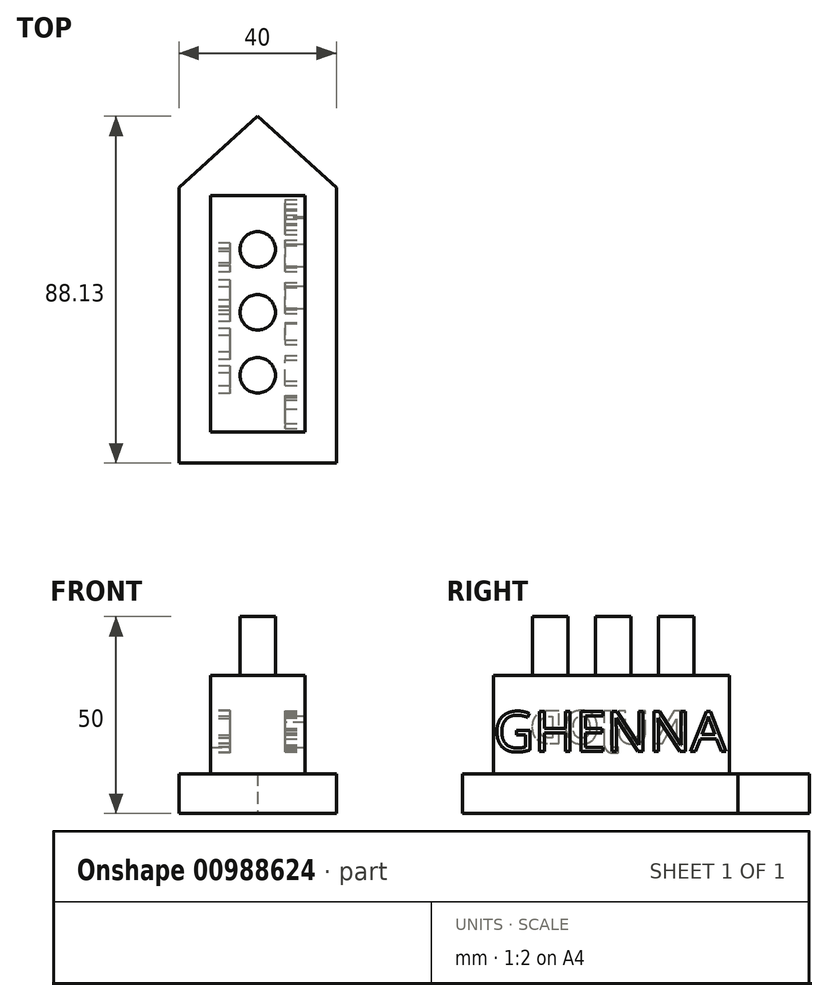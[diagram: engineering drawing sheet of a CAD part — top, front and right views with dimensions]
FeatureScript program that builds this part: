
annotation { "Feature Type Name" : "Feature", "Feature Type Description" : "" }
export const myFeature = defineFeature(function(context is Context, id is Id, definition is map)
    precondition{}
    {
        {
            var Q0;
            Q0=qCreatedBy(makeId("Top.planeOp"),FACE);
            var sketch = newSketch(context, id + "F0", { "sketchPlane" : qUnion([Q0])});
            skLineSegment(sketch, "E0", {"start": v(-20, 21.16) * mm, "end": v(-20, -48.84) * mm});
            skLineSegment(sketch, "E1", {"start": v(-20, -48.84) * mm, "end": v(20, -48.84) * mm});
            skLineSegment(sketch, "E2", {"start": v(20, -48.84) * mm, "end": v(20, 21.16) * mm});
            skLineSegment(sketch, "E3", {"start": v(-20, 21.16) * mm, "end": v(0, 39.3) * mm});
            skLineSegment(sketch, "E4", {"start": v(0, 39.3) * mm, "end": v(20, 21.16) * mm});
            skSolve(sketch);
        }
        {
            var Q0;
            Q0 = qSketchRegion(id + "F0", true);
            extrude(context, id + "F1", {"entities" : qUnion([Q0]), "depth" : 10 * mm, "offsetDistance" : 25 * mm});
        }
        {
            var Q0;
            Q0=makeQuery(id+"F1.opExtrude","CAP_FACE",FACE,{"disambiguationData":[OSD([sQuery(id+"F0.wireOp",EDGE,"E0"),sQuery(id+"F0.wireOp",EDGE,"E1"),sQuery(id+"F0.wireOp",EDGE,"E2"),sQuery(id+"F0.wireOp",EDGE,"E3"),sQuery(id+"F0.wireOp",EDGE,"E4")])],"isStart":false});
            var sketch = newSketch(context, id + "F2", { "sketchPlane" : qUnion([Q0])});
            skLineSegment(sketch, "E5", {"start": v(-12, 19.07) * mm, "end": v(-12, -40.93) * mm});
            skLineSegment(sketch, "E6", {"start": v(-12, -40.93) * mm, "end": v(12, -40.93) * mm});
            skLineSegment(sketch, "E7", {"start": v(12, -40.93) * mm, "end": v(12, 19.07) * mm});
            skLineSegment(sketch, "E8", {"start": v(12, 19.07) * mm, "end": v(-12, 19.07) * mm});
            skSolve(sketch);
        }
        {
            var Q0;
            Q0 = qSketchRegion(id + "F2", true);
            extrude(context, id + "F3", {"entities" : qUnion([Q0]), "operationType" : NewBodyOperationType.ADD, "depth" : 25 * mm, "offsetDistance" : 25 * mm});
        }
        {
            var Q0;
            Q0=makeQuery(id+"F3.opExtrude","CAP_FACE",FACE,{"disambiguationData":[OSD([sQuery(id+"F2.wireOp",EDGE,"E5"),sQuery(id+"F2.wireOp",EDGE,"E6"),sQuery(id+"F2.wireOp",EDGE,"E7"),sQuery(id+"F2.wireOp",EDGE,"E8")])],"isStart":false});
            var sketch = newSketch(context, id + "F4", { "sketchPlane" : qUnion([Q0])});
            skCircle(sketch, "E9", {"center": v(0, 5.44) * mm, "radius": 4.5 * mm});
            skCircle(sketch, "E10", {"center": v(0, -10.56) * mm, "radius": 4.5 * mm});
            skCircle(sketch, "E11", {"center": v(0, -26.56) * mm, "radius": 4.5 * mm});
            skSolve(sketch);
        }
        {
            var Q0;
            Q0 = qSketchRegion(id + "F4", true);
            extrude(context, id + "F5", {"entities" : qUnion([Q0]), "depth" : 15 * mm, "offsetDistance" : 25 * mm});
        }
        {
            var Q0;
            Q0=makeQuery(id+"F3.opExtrude","SWEPT_FACE",FACE,{"disambiguationData":[OSD([sQuery(id+"F2.wireOp",EDGE,"E5")])]});
            var sketch = newSketch(context, id + "F6", { "sketchPlane" : qUnion([Q0])});
            skText(sketch, "E12", { "text": "NUJOD", "fontName": "OpenSans-Bold.ttf"});
            const initialGuessF6  = {"E12": [-0.00811, 0.01773, 1, 0, 0.00836]};
            skSetInitialGuess(sketch, initialGuessF6);
            skSolve(sketch);
        }
        {
            var Q0;
            Q0=makeQuery(id+"F3.opExtrude","SWEPT_FACE",FACE,{"disambiguationData":[OSD([sQuery(id+"F2.wireOp",EDGE,"E7")])]});
            var sketch = newSketch(context, id + "F7", { "sketchPlane" : qUnion([Q0])});
            skText(sketch, "E13", { "text": "GHENNA", "fontName": "OpenSans-Regular.ttf"});
            const initialGuessF7  = {"E13": [-0.04093, 0.01571, 1, 0, 0.01022]};
            skSetInitialGuess(sketch, initialGuessF7);
            skSolve(sketch);
        }
        {
            var Q0;
            Q0 = qSketchRegion(id + "F7", true);
            extrude(context, id + "F8", {"entities" : qUnion([Q0]), "operationType" : NewBodyOperationType.REMOVE, "oppositeDirection" : true, "depth" : 5 * mm, "offsetDistance" : 25 * mm});
        }
        {
            var Q0;
            Q0 = qSketchRegion(id + "F6", true);
            extrude(context, id + "F9", {"entities" : qUnion([Q0]), "operationType" : NewBodyOperationType.REMOVE, "oppositeDirection" : true, "depth" : 5 * mm, "offsetDistance" : 25 * mm});
        }
    });
